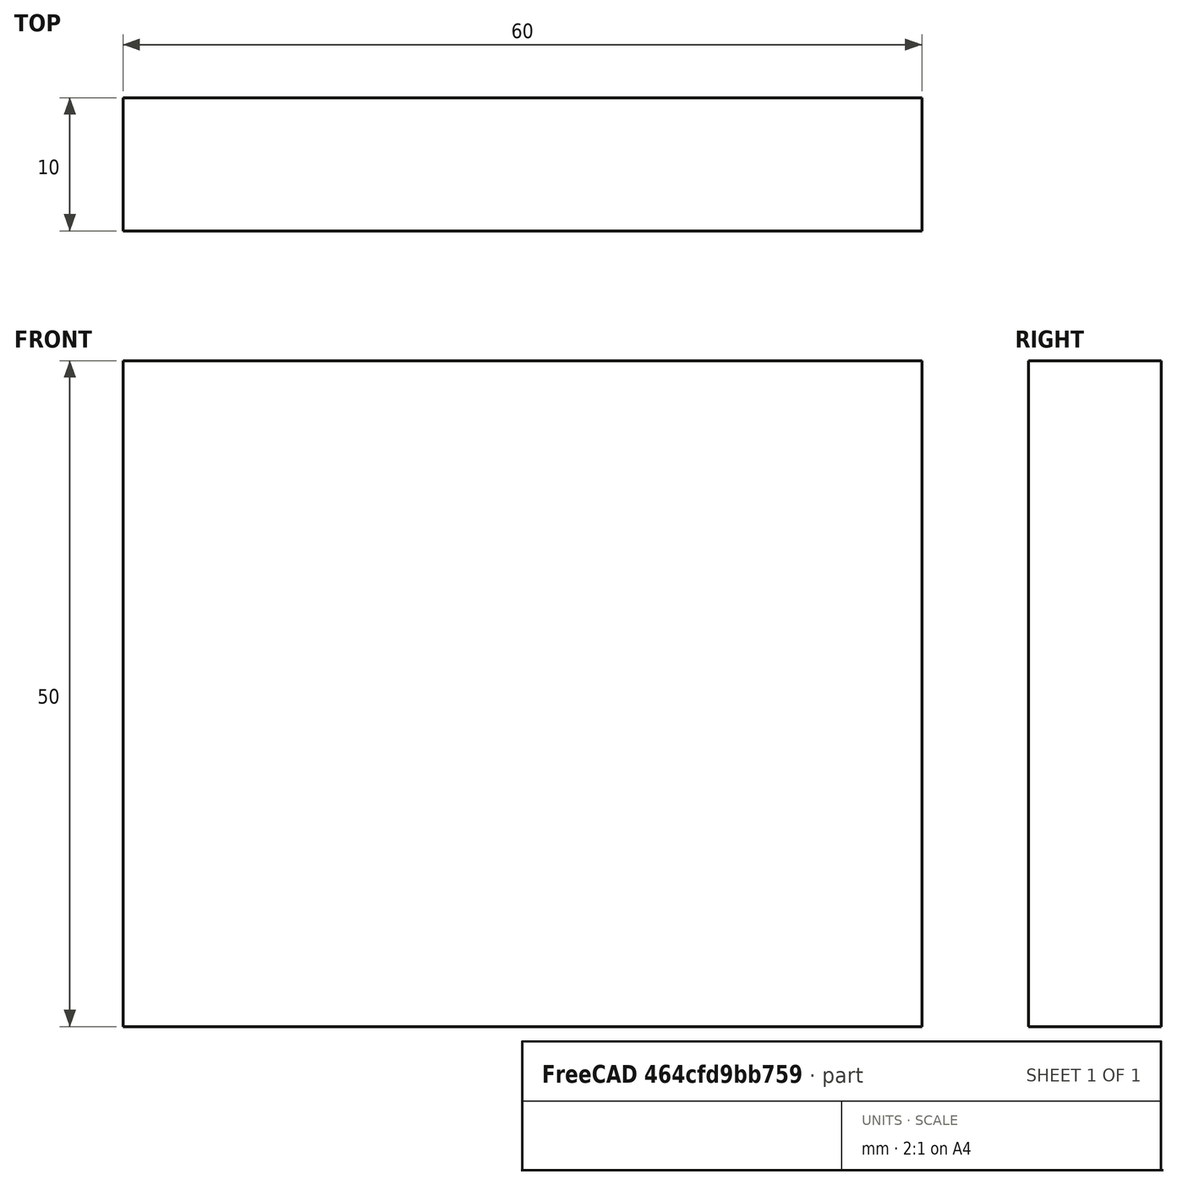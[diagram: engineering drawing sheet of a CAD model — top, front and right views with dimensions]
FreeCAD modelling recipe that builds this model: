
FCSTD DOCUMENT  (FreeCAD 0.15R4671 (Git))
Label: Flat Bar 60x10 EN10058 S235JR
License: All rights reserved
LicenseURL: http://en.wikipedia.org/wiki/All_rights_reserved
objects: Sketcher::SketchObject×1, Part::Extrusion×1
note: 2 computed .brp shape members not serialized (recipe doc carries the construction recipe); baked Part::Feature solids carry a one-line shape summary decoded from their .brp

FEATURE [Sketcher::SketchObject] Sketch
  sketch-geometry (4):
    g0: LineSegment StartX=-30 StartY=-5 StartZ=0 EndX=30 EndY=-5 EndZ=0
    g1: LineSegment StartX=30 StartY=-5 StartZ=0 EndX=30 EndY=5 EndZ=0
    g2: LineSegment StartX=30 StartY=5 StartZ=0 EndX=-30 EndY=5 EndZ=0
    g3: LineSegment StartX=-30 StartY=5 StartZ=0 EndX=-30 EndY=-5 EndZ=0
  constraints (12):
    c: Coincident(g0,g1)
    c: Coincident(g1,g2)
    c: Coincident(g2,g3)
    c: Coincident(g3,g0)
    c: Horizontal(g0)
    c: Horizontal(g2)
    c: Vertical(g1)
    c: Vertical(g3)
    c: Symmetric(g1,g2,g-2)
    c: Symmetric(g0,g1,g-1)
    c: DistanceY(g1) = 10
    c: DistanceX(g0) = 60
FEATURE [Part::Extrusion] Extrude  label="Flat Bar 60x10 EN10058 S235JR"
  Base = -> Sketch
  Dir = (0,0,50)
  Solid = true
